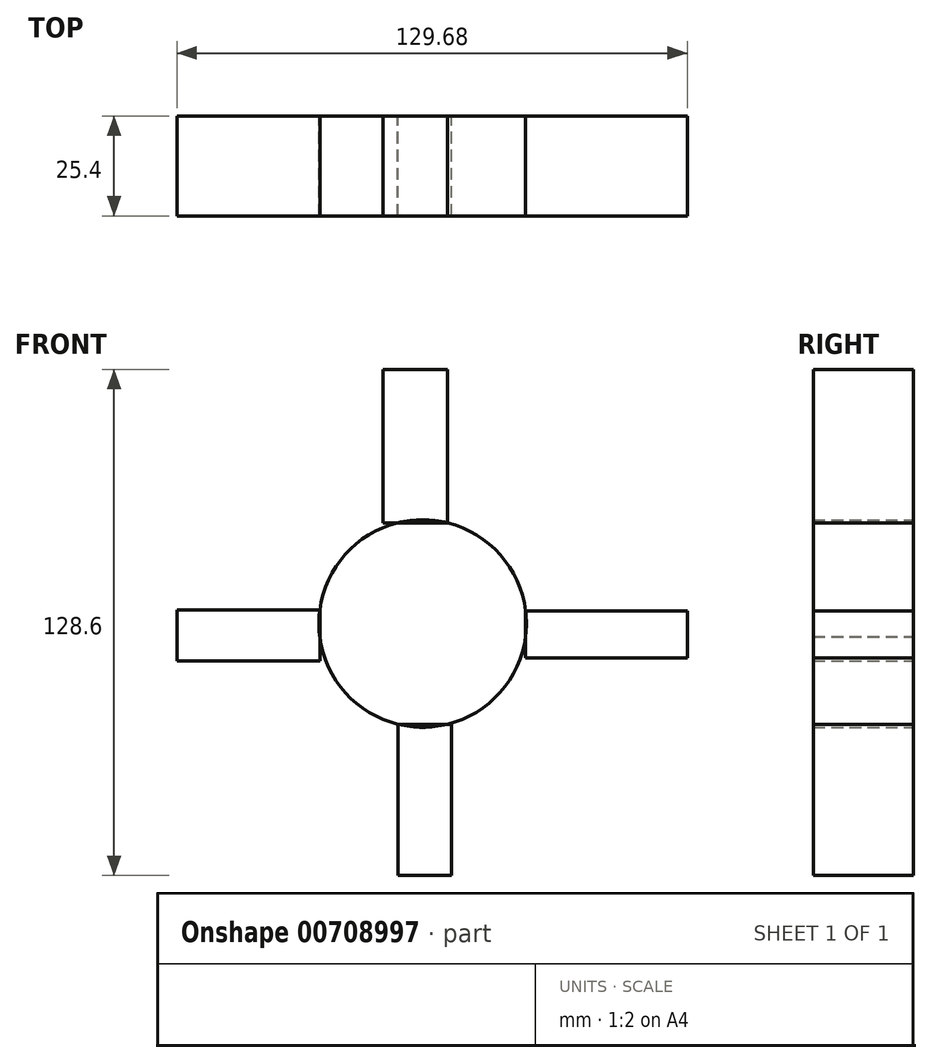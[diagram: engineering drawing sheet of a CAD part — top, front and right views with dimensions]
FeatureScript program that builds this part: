
annotation { "Feature Type Name" : "Feature", "Feature Type Description" : "" }
export const myFeature = defineFeature(function(context is Context, id is Id, definition is map)
    precondition{}
    {
        {
            var Q0;
            Q0=qCreatedBy(makeId("Front.planeOp"),FACE);
            var sketch = newSketch(context, id + "F0", { "sketchPlane" : qUnion([Q0])});
            skCircle(sketch, "E0", {"center": v(0, 0) * mm, "radius": 26.35 * mm});
            skLineSegment(sketch, "E1.bottom", {"start": v(6.39, 25.57) * mm, "end": v(-10.07, 25.57) * mm});
            skLineSegment(sketch, "E1.top", {"start": v(6.39, 64.57) * mm, "end": v(-10.07, 64.57) * mm});
            skLineSegment(sketch, "E1.left", {"start": v(6.39, 25.57) * mm, "end": v(6.39, 64.57) * mm});
            skLineSegment(sketch, "E1.right", {"start": v(-10.07, 25.57) * mm, "end": v(-10.07, 64.57) * mm});
            skLineSegment(sketch, "E2.bottom", {"start": v(26.15, 3.25) * mm, "end": v(67.26, 3.25) * mm});
            skLineSegment(sketch, "E2.top", {"start": v(26.15, -8.73) * mm, "end": v(67.26, -8.73) * mm});
            skLineSegment(sketch, "E2.left", {"start": v(26.15, 3.25) * mm, "end": v(26.15, -8.73) * mm});
            skLineSegment(sketch, "E2.right", {"start": v(67.26, 3.25) * mm, "end": v(67.26, -8.73) * mm});
            skLineSegment(sketch, "E3.bottom", {"start": v(-26.12, 3.46) * mm, "end": v(-62.42, 3.46) * mm});
            skLineSegment(sketch, "E3.top", {"start": v(-26.12, -9.53) * mm, "end": v(-62.42, -9.53) * mm});
            skLineSegment(sketch, "E3.left", {"start": v(-26.12, 3.46) * mm, "end": v(-26.12, -9.53) * mm});
            skLineSegment(sketch, "E3.right", {"start": v(-62.42, 3.46) * mm, "end": v(-62.42, -9.53) * mm});
            skLineSegment(sketch, "E4.bottom", {"start": v(-6.23, -25.6) * mm, "end": v(7.38, -25.6) * mm});
            skLineSegment(sketch, "E4.top", {"start": v(-6.23, -64.03) * mm, "end": v(7.38, -64.03) * mm});
            skLineSegment(sketch, "E4.left", {"start": v(-6.23, -25.6) * mm, "end": v(-6.23, -64.03) * mm});
            skLineSegment(sketch, "E4.right", {"start": v(7.38, -25.6) * mm, "end": v(7.38, -64.03) * mm});
            skSolve(sketch);
        }
        {
            var Q0;
            {var subQ0=sQuery(id+"F0.wireOp",EDGE,"E4.bottom");var subQ1=sQuery(id+"F0.wireOp",EDGE,"E0");var subQ2=makeQuery(id+"F0.imprint","INTERSECT",VERTEX,{"derivedFrom":[subQ1,subQ0]});Q0=makeQuery(id+"F0.imprint","IMPRINT",FACE,{"disambiguationData":[TD([[makeQuery(id+"F0.imprint","IMPRINT",EDGE,{"disambiguationData":[TD([[subQ2,-1.0]])],"derivedFrom":subQ1}),1.0]])]});}
            var Q1;
            Q1=makeQuery(id+"F0.imprint","IMPRINT",FACE,{"disambiguationData":[TD([[makeQuery(id+"F0.imprint","IMPRINT",EDGE,{"derivedFrom":sQuery(id+"F0.wireOp",EDGE,"E1.top")}),1.0]])]});
            var Q2;
            {var subQ4=sQuery(id+"F0.wireOp",EDGE,"E3.bottom");Q2=makeQuery(id+"F0.imprint","IMPRINT",FACE,{"disambiguationData":[TD([[makeQuery(id+"F0.imprint","IMPRINT",EDGE,{"derivedFrom":subQ4}),1.0]])]});}
            var Q3;
            {var subQ4=sQuery(id+"F0.wireOp",EDGE,"E2.bottom");Q3=makeQuery(id+"F0.imprint","IMPRINT",FACE,{"disambiguationData":[TD([[makeQuery(id+"F0.imprint","IMPRINT",EDGE,{"derivedFrom":subQ4}),-1.0]])]});}
            var Q4;
            Q4=makeQuery(id+"F0.imprint","IMPRINT",FACE,{"disambiguationData":[TD([[makeQuery(id+"F0.imprint","IMPRINT",EDGE,{"derivedFrom":sQuery(id+"F0.wireOp",EDGE,"E4.top")}),1.0]])]});
            extrude(context, id + "F1", {"entities" : qUnion([Q0, Q1, Q2, Q3, Q4]), "depth" : 25.4 * mm, "offsetDistance" : 25.4 * mm});
        }
    });
